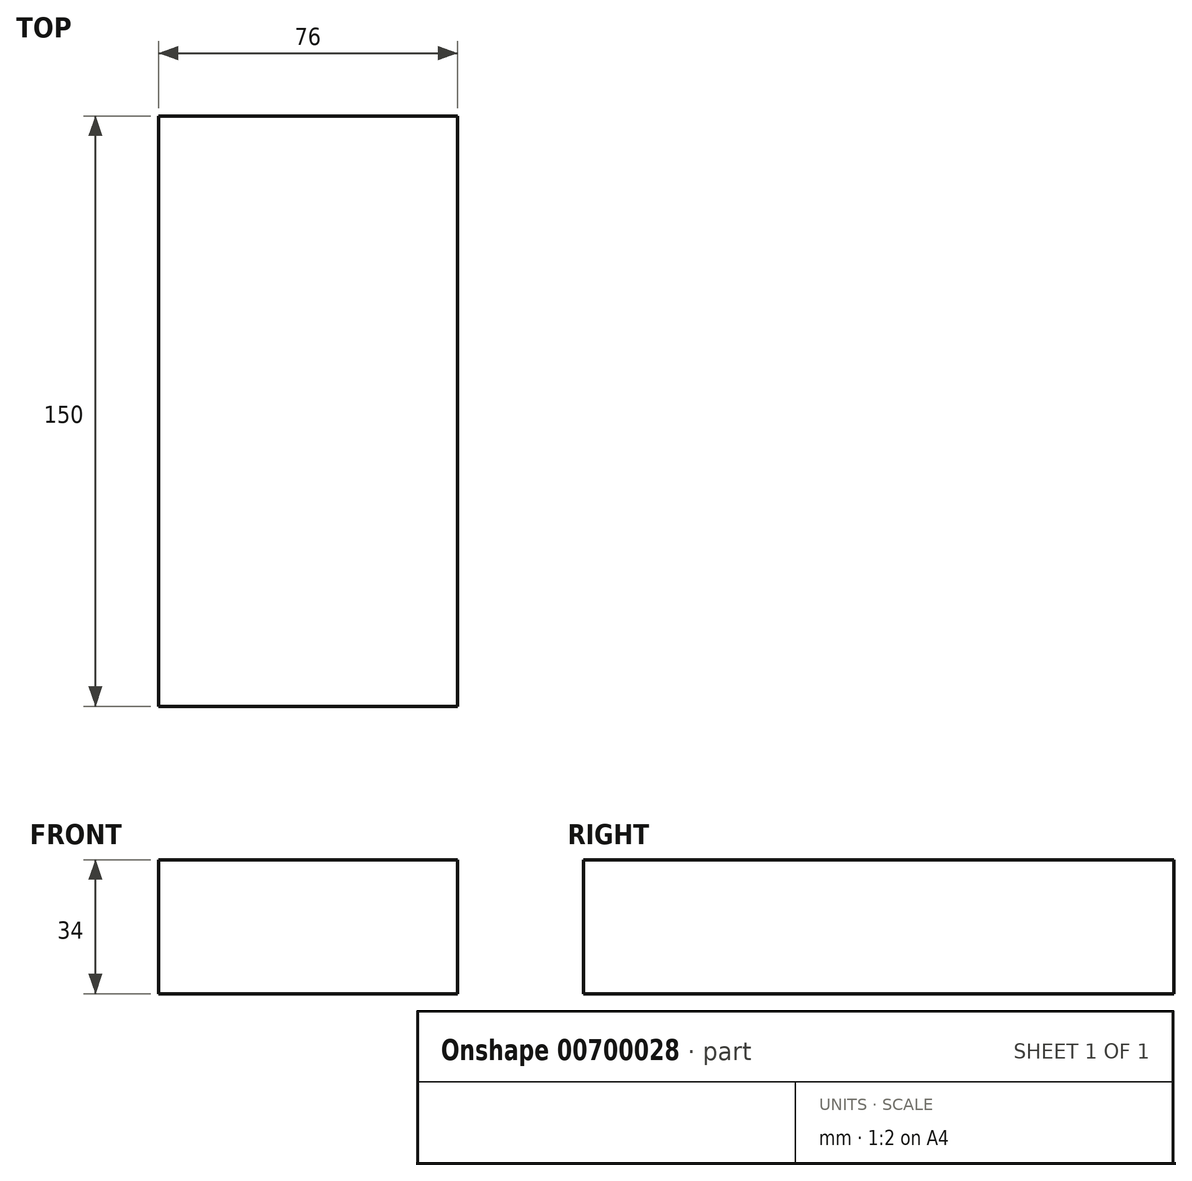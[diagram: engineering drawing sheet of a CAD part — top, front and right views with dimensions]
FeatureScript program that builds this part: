
annotation { "Feature Type Name" : "Feature", "Feature Type Description" : "" }
export const myFeature = defineFeature(function(context is Context, id is Id, definition is map)
    precondition{}
    {
        {
            var Q0;
            Q0=qCreatedBy(makeId("Top.planeOp"),FACE);
            var sketch = newSketch(context, id + "F0", { "sketchPlane" : qUnion([Q0])});
            skLineSegment(sketch, "E0.bottom", {"start": v(38, -75) * mm, "end": v(-38, -75) * mm});
            skLineSegment(sketch, "E0.top", {"start": v(38, 75) * mm, "end": v(-38, 75) * mm});
            skLineSegment(sketch, "E0.left", {"start": v(38, -75) * mm, "end": v(38, 75) * mm});
            skLineSegment(sketch, "E0.right", {"start": v(-38, -75) * mm, "end": v(-38, 75) * mm});
            skPoint(sketch, "E0.middle", {"position": v(0, 0) * mm});
            skSolve(sketch);
        }
        {
            var Q0;
            Q0 = qSketchRegion(id + "F0", true);
            extrude(context, id + "F1", {"entities" : qUnion([Q0]), "depth" : 34 * mm, "offsetDistance" : 25 * mm});
        }
    });
